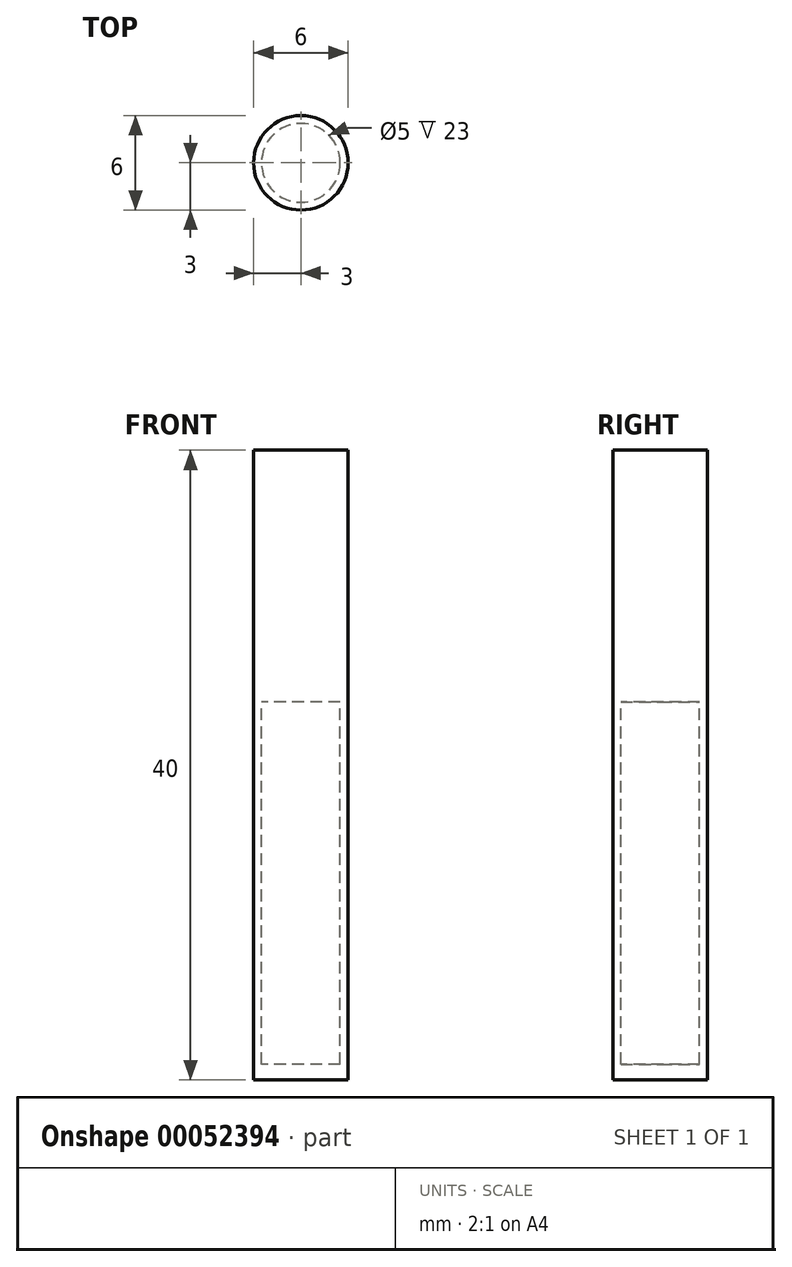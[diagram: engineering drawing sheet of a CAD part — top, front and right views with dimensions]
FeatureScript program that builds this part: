
annotation { "Feature Type Name" : "Feature", "Feature Type Description" : "" }
export const myFeature = defineFeature(function(context is Context, id is Id, definition is map)
    precondition{}
    {
        {
            var Q0;
            Q0=qCreatedBy(makeId("Top.planeOp"),FACE);
            var sketch = newSketch(context, id + "F0", { "sketchPlane" : qUnion([Q0])});
            skCircle(sketch, "E0", {"center": v(0, 0) * mm, "radius": 3 * mm});
            skSolve(sketch);
        }
        {
            var Q0;
            Q0 = qSketchRegion(id + "F0", true);
            var Q1;
            Q1=sQuery(id+"F0.wireOp",EDGE,"E0");
            extrude(context, id + "F1", {"entities" : qUnion([Q0]), "surfaceEntities" : qUnion([Q1]), "depth" : 28 * mm, "hasSecondDirection" : true, "secondDirectionOppositeDirection" : true, "secondDirectionDepth" : 12 * mm});
        }
        {
            var Q0;
            Q0=qCreatedBy(makeId("Top.planeOp"),FACE);
            var sketch = newSketch(context, id + "F2", { "sketchPlane" : qUnion([Q0])});
            skCircle(sketch, "E1", {"center": v(0, 0) * mm, "radius": 2.5 * mm});
            skSolve(sketch);
        }
        {
            var Q0;
            Q0 = qSketchRegion(id + "F2", true);
            extrude(context, id + "F3", {"entities" : qUnion([Q0]), "operationType" : NewBodyOperationType.REMOVE, "oppositeDirection" : true, "depth" : 11 * mm, "hasSecondDirection" : true, "secondDirectionOppositeDirection" : false, "secondDirectionDepth" : 12 * mm});
        }
    });
